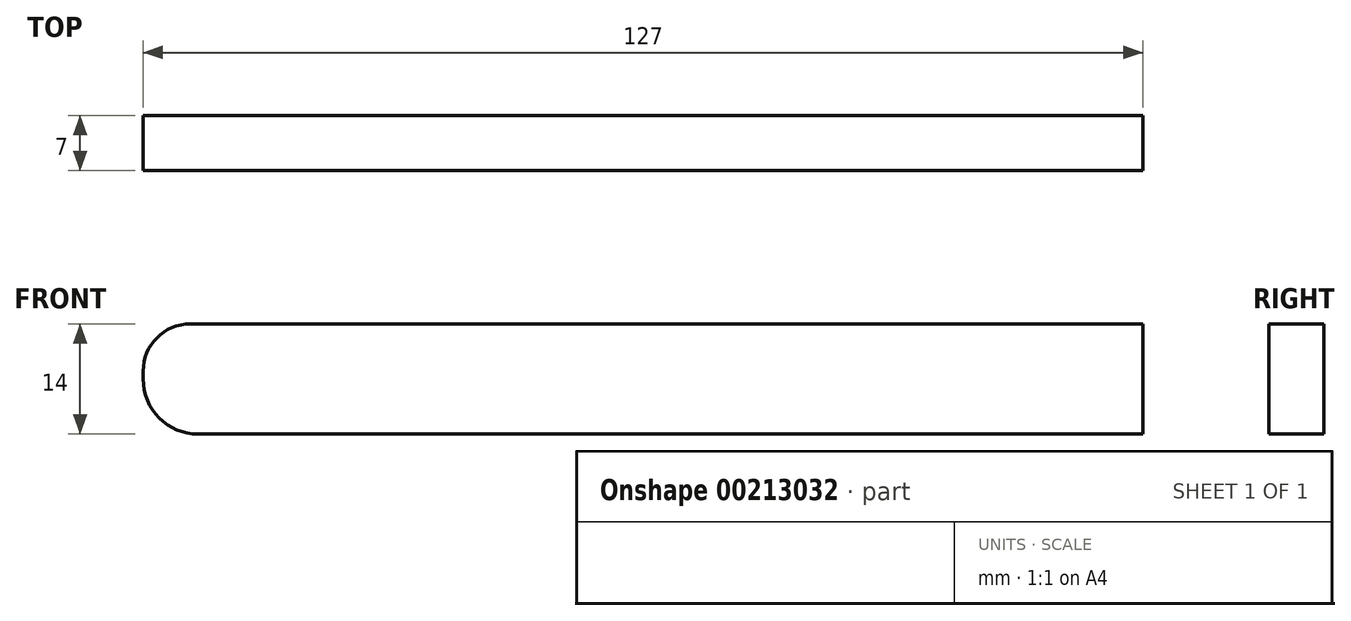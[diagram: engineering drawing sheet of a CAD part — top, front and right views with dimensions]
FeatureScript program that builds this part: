
annotation { "Feature Type Name" : "Feature", "Feature Type Description" : "" }
export const myFeature = defineFeature(function(context is Context, id is Id, definition is map)
    precondition{}
    {
        {
            var Q0;
            Q0=qCreatedBy(makeId("Front.planeOp"),FACE);
            var sketch = newSketch(context, id + "F0", { "sketchPlane" : qUnion([Q0])});
            skLineSegment(sketch, "E0.bottom", {"start": v(0, 0) * mm, "end": v(127, 0) * mm});
            skLineSegment(sketch, "E0.top", {"start": v(0, 14) * mm, "end": v(127, 14) * mm});
            skLineSegment(sketch, "E0.left", {"start": v(0, 0) * mm, "end": v(0, 14) * mm});
            skLineSegment(sketch, "E0.right", {"start": v(127, 0) * mm, "end": v(127, 14) * mm});
            skSolve(sketch);
        }
        {
            var Q0;
            Q0 = qSketchRegion(id + "F0", true);
            extrude(context, id + "F1", {"entities" : qUnion([Q0]), "depth" : 7 * mm});
        }
        {
            var Q0;
            Q0=makeQuery(id+"F1.opExtrude","SWEPT_EDGE",EDGE,{"disambiguationData":[OSD([sQuery(id+"F0.wireOp",EDGE,"E0.top"),sQuery(id+"F0.wireOp",EDGE,"E0.left")])]});
            fillet(context, id + "F2", {"entities" : qUnion([Q0]), "radius" : 6 * mm, "tangentPropagation" : true, "allowEdgeOverflow" : false});
        }
        {
            var Q0;
            Q0=makeQuery(id+"F1.opExtrude","SWEPT_EDGE",EDGE,{"disambiguationData":[OSD([sQuery(id+"F0.wireOp",EDGE,"E0.bottom"),sQuery(id+"F0.wireOp",EDGE,"E0.left")])]});
            fillet(context, id + "F3", {"entities" : qUnion([Q0]), "radius" : 7 * mm, "tangentPropagation" : true, "allowEdgeOverflow" : false});
        }
    });
